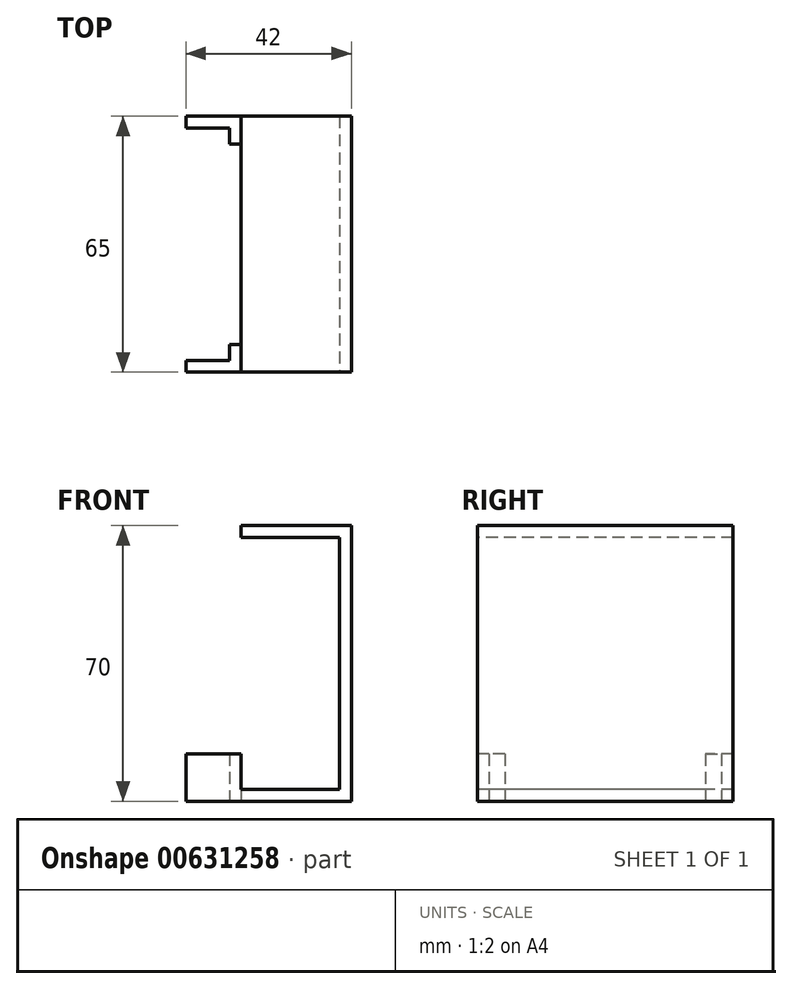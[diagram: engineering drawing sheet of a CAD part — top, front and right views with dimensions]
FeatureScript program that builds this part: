
annotation { "Feature Type Name" : "Feature", "Feature Type Description" : "" }
export const myFeature = defineFeature(function(context is Context, id is Id, definition is map)
    precondition{}
    {
        {
            var Q0;
            Q0=qCreatedBy(makeId("Top.planeOp"),FACE);
            var sketch = newSketch(context, id + "F0", { "sketchPlane" : qUnion([Q0])});
            skLineSegment(sketch, "E0.bottom", {"start": v(-12.5, 32.5) * mm, "end": v(12.5, 32.5) * mm});
            skLineSegment(sketch, "E0.top", {"start": v(-12.5, -32.5) * mm, "end": v(12.5, -32.5) * mm});
            skLineSegment(sketch, "E0.right", {"start": v(12.5, 32.5) * mm, "end": v(12.5, -32.5) * mm});
            skPoint(sketch, "E0.middle", {"position": v(0, 0) * mm});
            skLineSegment(sketch, "E1", {"start": v(12.5, 32.5) * mm, "end": v(15.5, 32.5) * mm});
            skLineSegment(sketch, "E2", {"start": v(15.5, 32.5) * mm, "end": v(15.5, -32.5) * mm});
            skLineSegment(sketch, "E3", {"start": v(15.5, -32.5) * mm, "end": v(12.5, -32.5) * mm});
            skLineSegment(sketch, "E4", {"start": v(-12.5, 32.5) * mm, "end": v(-12.5, -32.5) * mm});
            skLineSegment(sketch, "E5", {"start": v(-12.5, 32.5) * mm, "end": v(-26.5, 32.5) * mm});
            skLineSegment(sketch, "E6", {"start": v(-26.5, -32.5) * mm, "end": v(-12.5, -32.5) * mm});
            skLineSegment(sketch, "E7", {"start": v(-12.5, -32.5) * mm, "end": v(-12.5, -25.5) * mm});
            skLineSegment(sketch, "E8", {"start": v(-12.5, -25.5) * mm, "end": v(-15.5, -25.5) * mm});
            skLineSegment(sketch, "E9", {"start": v(-15.5, -25.5) * mm, "end": v(-15.5, -29.5) * mm});
            skLineSegment(sketch, "E10.MirrorCS", {"start": v(-15.5, 25.5) * mm, "end": v(-15.5, 29.5) * mm});
            skLineSegment(sketch, "E11.MirrorCS", {"start": v(-12.5, 25.5) * mm, "end": v(-15.5, 25.5) * mm});
            skLineSegment(sketch, "E12.MirrorCS", {"start": v(-12.5, 32.5) * mm, "end": v(-12.5, 25.5) * mm});
            skLineSegment(sketch, "E13.MirrorCS", {"start": v(-26.5, 32.5) * mm, "end": v(-12.5, 32.5) * mm});
            skCircle(sketch, "E14", {"center": v(-19.5, -24.5) * mm, "radius": 2 * mm});
            skPoint(sketch, "E14.perimeterSnap0", {"position": v(-19.5, -29.5) * mm});
            skCircle(sketch, "E15", {"center": v(-19.5, 24.5) * mm, "radius": 2 * mm});
            skLineSegment(sketch, "E16", {"start": v(-26.5, 32.5) * mm, "end": v(-26.5, -32.5) * mm});
            skLineSegment(sketch, "E17", {"start": v(-26.5, 29.5) * mm, "end": v(-26.5, 32.5) * mm});
            skLineSegment(sketch, "E18", {"start": v(-15.5, -29.5) * mm, "end": v(-26.5, -29.5) * mm});
            skLineSegment(sketch, "E19", {"start": v(-26.5, -29.5) * mm, "end": v(-26.5, -32.5) * mm});
            skLineSegment(sketch, "E20", {"start": v(-15.5, 29.5) * mm, "end": v(-26.5, 29.5) * mm});
            skSolve(sketch);
        }
        {
            var Q0;
            Q0=makeQuery(id+"F0.imprint","IMPRINT",FACE,{"disambiguationData":[TD([[makeQuery(id+"F0.imprint","IMPRINT",EDGE,{"derivedFrom":sQuery(id+"F0.wireOp",EDGE,"E10.MirrorCS")}),-1.0]])]});
            var Q1;
            Q1=makeQuery(id+"F0.imprint","IMPRINT",FACE,{"disambiguationData":[TD([[makeQuery(id+"F0.imprint","IMPRINT",EDGE,{"derivedFrom":sQuery(id+"F0.wireOp",EDGE,"E6")}),1.0]])]});
            extrude(context, id + "F1", {"entities" : qUnion([Q0, Q1]), "depth" : 12 * mm, "offsetDistance" : 25 * mm});
        }
        {
            var Q0;
            Q0=makeQuery(id+"F0.imprint","IMPRINT",FACE,{"disambiguationData":[TD([[makeQuery(id+"F0.imprint","IMPRINT",EDGE,{"derivedFrom":sQuery(id+"F0.wireOp",EDGE,"E4")}),-1.0]])]});
            extrude(context, id + "F2", {"entities" : qUnion([Q0]), "operationType" : NewBodyOperationType.ADD, "depth" : 3 * mm, "offsetDistance" : 25 * mm});
        }
        {
            var Q0;
            Q0=makeQuery(id+"F0.imprint","IMPRINT",FACE,{"disambiguationData":[TD([[makeQuery(id+"F0.imprint","IMPRINT",EDGE,{"derivedFrom":sQuery(id+"F0.wireOp",EDGE,"E0.bottom")}),-1.0]])]});
            extrude(context, id + "F3", {"entities" : qUnion([Q0]), "operationType" : NewBodyOperationType.ADD, "depth" : 3 * mm, "offsetDistance" : 25 * mm});
        }
        {
            var Q0;
            Q0=makeQuery(id+"F0.imprint","IMPRINT",FACE,{"disambiguationData":[TD([[makeQuery(id+"F0.imprint","IMPRINT",EDGE,{"derivedFrom":sQuery(id+"F0.wireOp",EDGE,"E0.right")}),1.0]])]});
            extrude(context, id + "F4", {"entities" : qUnion([Q0]), "operationType" : NewBodyOperationType.ADD, "depth" : 70 * mm, "offsetDistance" : 25 * mm});
        }
        {
            var Q0;
            Q0=makeQuery(id+"F4.opExtrude","SWEPT_FACE",FACE,{"disambiguationData":[OSD([sQuery(id+"F0.wireOp",EDGE,"E0.right")])]});
            var sketch = newSketch(context, id + "F5", { "sketchPlane" : qUnion([Q0])});
            skLineSegment(sketch, "E21", {"start": v(-32.5, 70) * mm, "end": v(-32.5, 67) * mm});
            skLineSegment(sketch, "E22", {"start": v(-32.5, 67) * mm, "end": v(32.5, 67) * mm});
            skLineSegment(sketch, "E23", {"start": v(32.5, 67) * mm, "end": v(32.5, 70) * mm});
            skLineSegment(sketch, "E24", {"start": v(32.5, 70) * mm, "end": v(-32.5, 70) * mm});
            skSolve(sketch);
        }
        {
            var Q0;
            Q0=makeQuery(id+"F5.imprint","IMPRINT",FACE,{"disambiguationData":[TD([[makeQuery(id+"F5.imprint","IMPRINT",EDGE,{"derivedFrom":sQuery(id+"F5.wireOp",EDGE,"E21")}),1.0]])]});
            extrude(context, id + "F6", {"entities" : qUnion([Q0]), "operationType" : NewBodyOperationType.ADD, "depth" : 25 * mm, "offsetDistance" : 25 * mm});
        }
    });
